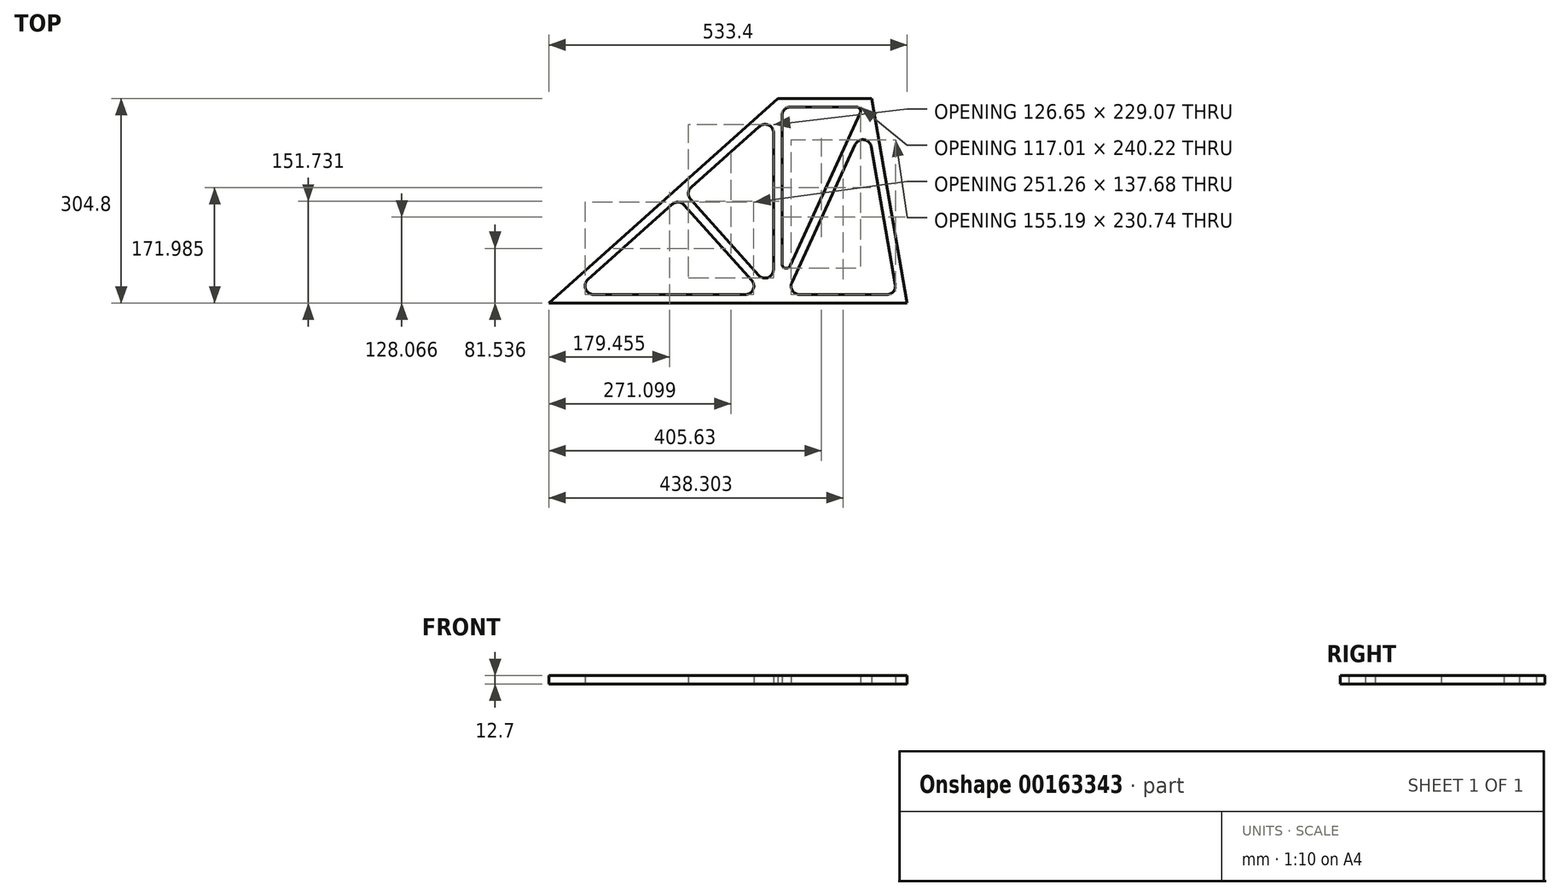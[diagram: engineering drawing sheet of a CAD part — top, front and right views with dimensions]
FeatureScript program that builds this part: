
annotation { "Feature Type Name" : "Feature", "Feature Type Description" : "" }
export const myFeature = defineFeature(function(context is Context, id is Id, definition is map)
    precondition{}
    {
        {
            var Q0;
            Q0=qCreatedBy(makeId("Top.planeOp"),FACE);
            var sketch = newSketch(context, id + "F0", { "sketchPlane" : qUnion([Q0])});
            skLineSegment(sketch, "E0", {"start": v(-121, -34.8) * mm, "end": v(412.4, -34.8) * mm});
            skLineSegment(sketch, "E1", {"start": v(-121, -34.8) * mm, "end": v(219.79, 270) * mm});
            skLineSegment(sketch, "E2", {"start": v(219.79, 270) * mm, "end": v(359.51, 270) * mm});
            skLineSegment(sketch, "E3", {"start": v(359.51, 270) * mm, "end": v(412.4, -34.8) * mm});
            skPoint(sketch, "E4.visualSharp", {"position": v(-51.78, 10.07) * mm});
            skPoint(sketch, "E5.visualSharp", {"position": v(-47.05, 14.3) * mm});
            skPoint(sketch, "E6.visualSharp", {"position": v(-3.99, 52.82) * mm});
            skPoint(sketch, "E7.visualSharp", {"position": v(2.44, 55.72) * mm});
            skPoint(sketch, "E8.visualSharp", {"position": v(34.6, 55.72) * mm});
            skPoint(sketch, "E9.visualSharp", {"position": v(39.06, 50.02) * mm});
            skPoint(sketch, "E10.visualSharp", {"position": v(0.43, -23.24) * mm});
            skPoint(sketch, "E11.visualSharp", {"position": v(-6.14, -31.44) * mm});
            skPoint(sketch, "E12.visualSharp", {"position": v(-13.1, -33.18) * mm});
            skPoint(sketch, "E13.visualSharp", {"position": v(-100.13, -33.18) * mm});
            skPoint(sketch, "E14.visualSharp", {"position": v(3.04, -33.18) * mm});
            skPoint(sketch, "E15.visualSharp", {"position": v(53.5, -33.18) * mm});
            skLineSegment(sketch, "E16.0", {"start": v(-62.96, 0.07) * mm, "end": v(62.6, 112.37) * mm});
            skLineSegment(sketch, "E16.1", {"start": v(-54.5, -22.1) * mm, "end": v(171.5, -22.1) * mm});
            skLineSegment(sketch, "E16.2", {"start": v(359.08, 198.22) * mm, "end": v(394.73, -7.22) * mm});
            skLineSegment(sketch, "E16.3", {"start": v(238.84, 257.3) * mm, "end": v(336.8, 257.3) * mm});
            skLineSegment(sketch, "E17.0", {"start": v(191.27, 6.61) * mm, "end": v(90, 119.84) * mm});
            skLineSegment(sketch, "E17.1", {"start": v(213.44, 218.89) * mm, "end": v(213.44, 15.08) * mm});
            skLineSegment(sketch, "E18.1", {"start": v(226.14, 244.6) * mm, "end": v(226.14, 23.39) * mm});
            skLineSegment(sketch, "E19.trimOffspring", {"start": v(91, 137.77) * mm, "end": v(192.27, 228.36) * mm});
            skLineSegment(sketch, "E20.trimOffspring", {"start": v(180.98, -0.93) * mm, "end": v(80.53, 111.37) * mm});
            skLineSegment(sketch, "E21.trimOffspring", {"start": v(342.58, 248.3) * mm, "end": v(238.26, 20.74) * mm});
            skLineSegment(sketch, "E22.trimOffspring", {"start": v(335.02, 201.34) * mm, "end": v(240.84, -4.1) * mm});
            skLineSegment(sketch, "E23.trimOffspring", {"start": v(252.39, -22.1) * mm, "end": v(382.22, -22.1) * mm});
            skPoint(sketch, "E24.visualSharp", {"position": v(81.53, 129.3) * mm});
            skArc(sketch, "E24.filletArc", {"start": v(91, 137.77) * mm, "mid": v(86.78, 129.01) * mm, "end": v(90, 119.84) * mm});
            skPoint(sketch, "E25.visualSharp", {"position": v(72.06, 120.84) * mm});
            skArc(sketch, "E25.filletArc", {"start": v(80.53, 111.37) * mm, "mid": v(71.77, 115.59) * mm, "end": v(62.6, 112.37) * mm});
            skPoint(sketch, "E26.visualSharp", {"position": v(213.44, 247.29) * mm});
            skArc(sketch, "E26.filletArc", {"start": v(213.44, 218.89) * mm, "mid": v(205.92, 230.48) * mm, "end": v(192.27, 228.36) * mm});
            skPoint(sketch, "E27.visualSharp", {"position": v(226.14, 257.3) * mm});
            skArc(sketch, "E27.filletArc", {"start": v(238.84, 257.3) * mm, "mid": v(229.86, 253.59) * mm, "end": v(226.14, 244.6) * mm});
            skPoint(sketch, "E28.visualSharp", {"position": v(213.44, -18.17) * mm});
            skArc(sketch, "E28.filletArc", {"start": v(191.27, 6.61) * mm, "mid": v(205.27, 3.22) * mm, "end": v(213.44, 15.08) * mm});
            skPoint(sketch, "E29.visualSharp", {"position": v(199.9, -22.1) * mm});
            skArc(sketch, "E29.filletArc", {"start": v(171.5, -22.1) * mm, "mid": v(183.1, -14.58) * mm, "end": v(180.98, -0.93) * mm});
            skPoint(sketch, "E30.visualSharp", {"position": v(232.6, -22.1) * mm});
            skArc(sketch, "E30.filletArc", {"start": v(240.84, -4.1) * mm, "mid": v(241.7, -16.25) * mm, "end": v(252.39, -22.1) * mm});
            skPoint(sketch, "E31.visualSharp", {"position": v(397.32, -22.1) * mm});
            skArc(sketch, "E31.filletArc", {"start": v(382.22, -22.1) * mm, "mid": v(391.94, -17.57) * mm, "end": v(394.73, -7.22) * mm});
            skPoint(sketch, "E32.visualSharp", {"position": v(352.08, 238.56) * mm});
            skArc(sketch, "E32.filletArc", {"start": v(359.08, 198.22) * mm, "mid": v(348.2, 208.65) * mm, "end": v(335.02, 201.34) * mm});
            skPoint(sketch, "E33.visualSharp", {"position": v(-87.74, -22.1) * mm});
            skArc(sketch, "E33.filletArc", {"start": v(-62.96, 0.07) * mm, "mid": v(-66.36, -13.93) * mm, "end": v(-54.5, -22.1) * mm});
            skPoint(sketch, "E34.visualSharp", {"position": v(226.14, -5.7) * mm});
            skArc(sketch, "E34.filletArc", {"start": v(226.14, 23.39) * mm, "mid": v(231.13, 17.18) * mm, "end": v(238.26, 20.74) * mm});
            skPoint(sketch, "E35.visualSharp", {"position": v(346.7, 257.3) * mm});
            skArc(sketch, "E35.filletArc", {"start": v(342.58, 248.3) * mm, "mid": v(342.15, 254.38) * mm, "end": v(336.8, 257.3) * mm});
            skSolve(sketch);
        }
        {
            var Q0;
            Q0=makeQuery(id+"F0.imprint","IMPRINT",FACE,{"disambiguationData":[TD([[makeQuery(id+"F0.imprint","IMPRINT",EDGE,{"derivedFrom":sQuery(id+"F0.wireOp",EDGE,"E0")}),1.0]])]});
            extrude(context, id + "F1", {"entities" : qUnion([Q0]), "depth" : 12.7 * mm});
        }
    });
